# Revit family: Solo E-kahva
name_source: partatom
category: Casework
revit_build: Autodesk Revit 2015 (Build: 20140606_1530(x64)
units: mm (PartAtom-declared; Revit-internal decimal feet)

## types (3) — shared parameters
Depth = 235 mm  [stored 0.770997 ft]
Height = 235 mm  [stored 0.770997 ft]
Keynote = 1677
Manufacturer = Korpinen
Model = Solo E tukikahva
URL = http://www.korpinen.com
Width = 467 mm  [stored 1.53215 ft]
desired_width = 500 mm  [stored 1.64042 ft]
modular wall support = Modular wall support v : Modular support
rounding_radius = 30 mm  [stored 0.0984252 ft]
tube_diameter = 17 mm
wall_support_radius = 37 mm  [stored 0.121391 ft]
zero-valued in all types: NominalDepth, NominalHeight, NominalLength

## per-type parameters (varying)
| type | 1677 aluminum color |
| 1677W | valkoinen alumiini |
| 1677G | harmaa alumiini |
| 1677R | punainen alumiini |

note: [stored X ft] marks values corroborated as IEEE doubles in the binary element streams (Revit-internal decimal feet)

## geometry (parser evidence)
native form markers: Sweep x5
no freeform markers — native parametric forms only
